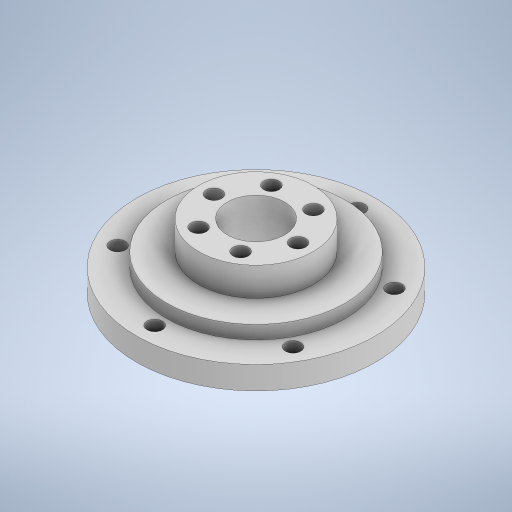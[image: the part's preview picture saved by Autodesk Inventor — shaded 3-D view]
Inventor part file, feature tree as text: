
AUTODESK INVENTOR PART (.ipt)
format: ipt  version: 2024 (Build 280153000, 153)  size: 345,088 bytes
history: native  units: mm
features: extrude x5, sketch x5, projected_geometry x3
ambient origin geometry x8: Origin, YZ Plane, XZ Plane, XY Plane, X Axis, Y Axis, Z Axis, Center Point
bodies: Solid1 (feature_tree)
feature tree (13):
  extrude  "Extrusion1"  Depth=106.0mm
  extrude  "Extrusion2"  Depth=12.0mm TaperAngle=0.0deg
  extrude  "Extrusion3"  Depth=8.0mm TaperAngle=0.0deg
  extrude  "Extrusion4"  Depth=22.0mm
  extrude  "Extrusion5"  Depth=7.0mm
  sketch  "Sketch1"  dims[d0=125.0mm d1=106.0mm]
  sketch  "Sketch2"  dims[d2=60.0mm d4=360.0deg d6=12.0mm d7=0.0mm]
  sketch  "Sketch3"  dims[d8=30.0mm d9=8.0mm d10=0.0mm]
  projected_geometry  "Projected Loop1"
  sketch  "Sketch4"  dims[d11=22.0mm d12=8.1mm]
  projected_geometry  "Projected Loop2"
  sketch  "Sketch5"  dims[d13=60.0mm d15=360.0deg d17=60.0mm d18=8.1mm d19=20.0mm d20=0.0mm d22=7.0mm d23=0.0mm d24=93.5mm d25=2.0mm d26=0.0mm]
  projected_geometry  "Projected Loop3"
